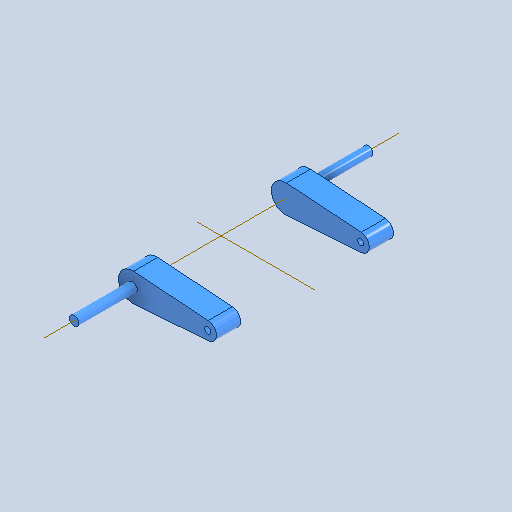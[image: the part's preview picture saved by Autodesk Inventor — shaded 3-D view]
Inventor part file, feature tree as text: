
AUTODESK INVENTOR PART (.ipt)
format: ipt  version: 2025 (Build 290162000, 162)  size: 155,648 bytes
history: native  units: mm
features: sketch x5, extrude x3, other x2, hole x2, plane x1, mirror x1
ambient origin geometry x8: Origin, YZ Plane, XZ Plane, XY Plane, X Axis, Y Axis, Z Axis, Center Point
bodies: Body1 (feature_tree)
feature tree (14):
  parser-record x1  (decoder bookkeeping rows leaked as tree rows — omitted from the tree; the rows remain in map.json)
  other  "實體1"
  plane  "工作平面1"
  extrude  "擠出1"  Depth=378.0mm
  extrude  "擠出2"  Depth=320.6953mm
  extrude  "擠出3"  Depth=120.0mm
  hole  "孔1"  [1 undecoded]
  hole  "孔3"  [1 undecoded]
  mirror  "鏡射1"
  sketch  "草圖1"
  sketch  "草圖2"
  sketch  "草圖3"
  sketch  "草圖5"
  sketch  "草圖8"
note: 2 required parameter values undecoded (feature->parameter linkage not recoverable at this tier; creation-order binding heuristic only, values carry confidence <= 0.55)
note: 1 file-system path scrubbed to <path> (originals preserved in map.json)
